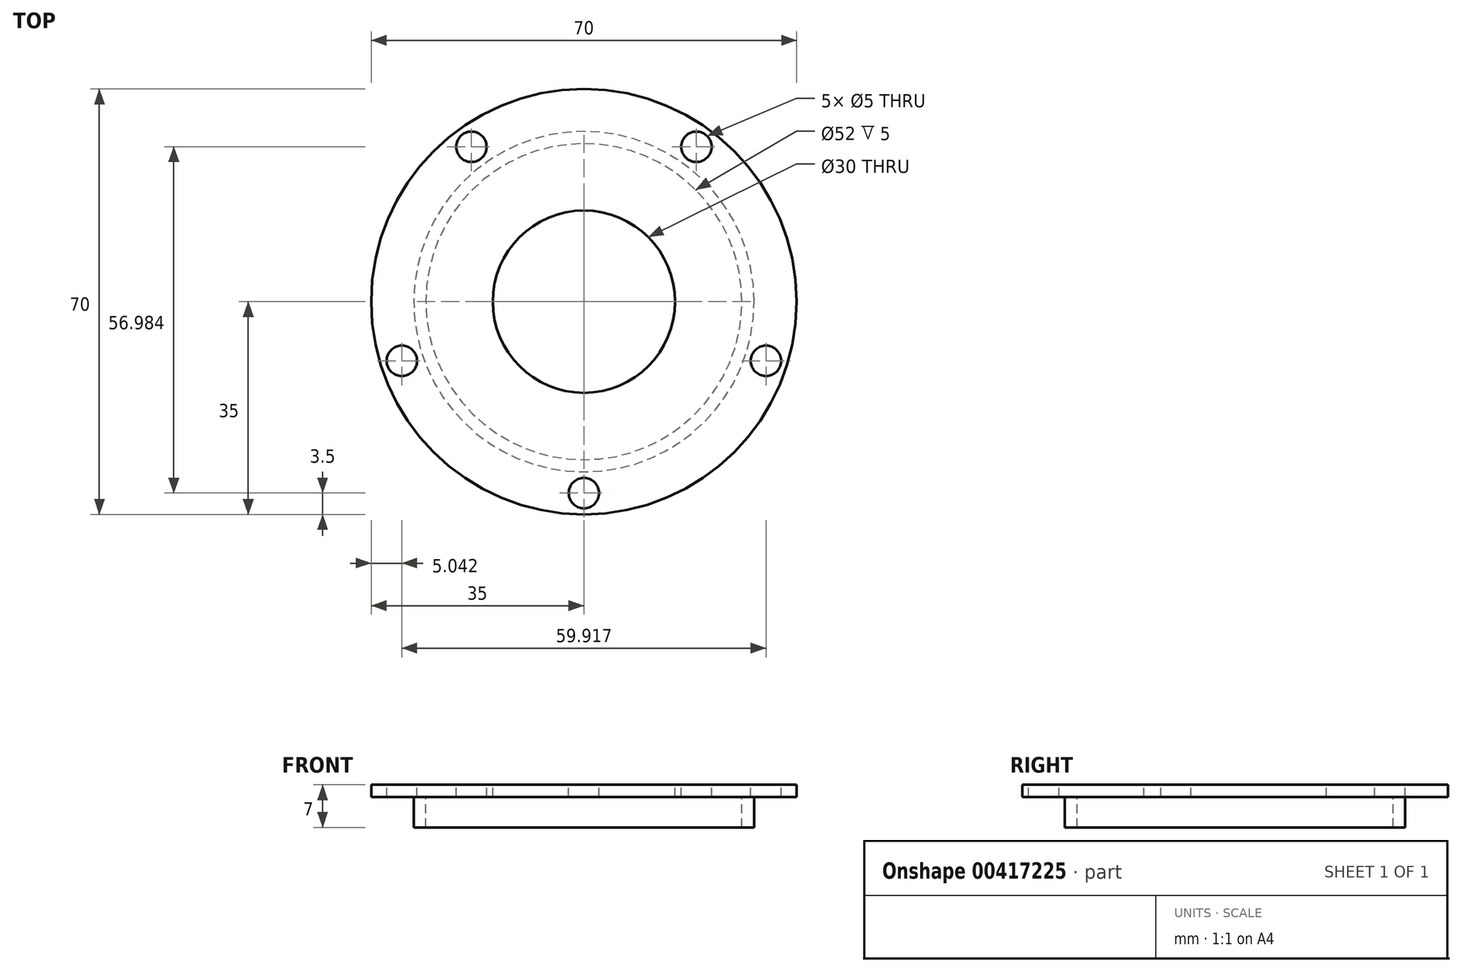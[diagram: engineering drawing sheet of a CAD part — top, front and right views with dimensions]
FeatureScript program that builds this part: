
annotation { "Feature Type Name" : "Feature", "Feature Type Description" : "" }
export const myFeature = defineFeature(function(context is Context, id is Id, definition is map)
    precondition{}
    {
        {
            var Q0;
            Q0=qCreatedBy(makeId("Front.planeOp"),FACE);
            var sketch = newSketch(context, id + "F0", { "sketchPlane" : qUnion([Q0])});
            skLineSegment(sketch, "E0", {"start": v(0, 9.86) * mm, "end": v(0, -12.44) * mm, "construction": true});
            skLineSegment(sketch, "E1", {"start": v(-35, 2) * mm, "end": v(-35, 0) * mm});
            skLineSegment(sketch, "E2", {"start": v(-35, 0) * mm, "end": v(-28, 0) * mm});
            skLineSegment(sketch, "E3", {"start": v(-28, 0) * mm, "end": v(-28, -5) * mm});
            skLineSegment(sketch, "E4", {"start": v(-28, -5) * mm, "end": v(-26, -5) * mm});
            skLineSegment(sketch, "E5", {"start": v(-26, -5) * mm, "end": v(-26, 0) * mm});
            skLineSegment(sketch, "E6", {"start": v(-26, 0) * mm, "end": v(-15, 0) * mm});
            skLineSegment(sketch, "E7", {"start": v(-15, 0) * mm, "end": v(-15, 2) * mm});
            skLineSegment(sketch, "E8", {"start": v(-15, 2) * mm, "end": v(-35, 2) * mm});
            skSolve(sketch);
        }
        {
            var Q0;
            Q0=makeQuery(id+"F0.imprint","IMPRINT",FACE,{"disambiguationData":[TD([[makeQuery(id+"F0.imprint","IMPRINT",EDGE,{"derivedFrom":sQuery(id+"F0.wireOp",EDGE,"E1")}),1.0]])]});
            var Q1;
            Q1=sQuery(id+"F0.wireOp",EDGE,"E0");
            revolve(context, id + "F1", {"entities" : qUnion([Q0]), "axis" : qUnion([Q1]), "revolveType" : RevolveType.FULL});
        }
        {
            var Q0;
            Q0=qCreatedBy(makeId("Top.planeOp"),FACE);
            var sketch = newSketch(context, id + "F2", { "sketchPlane" : qUnion([Q0])});
            skCircle(sketch, "E9", {"center": v(0, 0) * mm, "radius": 31.5 * mm, "construction": true});
            skPoint(sketch, "E10", {"position": v(0, -31.5) * mm});
            skPoint(sketch, "E11.1.0", {"position": v(29.96, -9.73) * mm});
            skPoint(sketch, "E11.2.0", {"position": v(18.52, 25.48) * mm});
            skPoint(sketch, "E11.3.0", {"position": v(-18.52, 25.48) * mm});
            skPoint(sketch, "E11.4.0", {"position": v(-29.96, -9.73) * mm});
            skSolve(sketch);
        }
        {
            var Q0;
            Q0=sQuery(id+"F2.wireOp",VERTEX,"E10");
            var Q1;
            Q1=sQuery(id+"F2.wireOp",VERTEX,"E11.4.0");
            var Q2;
            Q2=sQuery(id+"F2.wireOp",VERTEX,"E11.3.0");
            var Q3;
            Q3=sQuery(id+"F2.wireOp",VERTEX,"E11.2.0");
            var Q4;
            Q4=sQuery(id+"F2.wireOp",VERTEX,"E11.1.0");
            var Q5;
            Q5=makeQuery(id+"F1.opRevolve","SWEPT_BODY",BODY,{"disambiguationData":[OSD([sQuery(id+"F0.wireOp",EDGE,"E1"),sQuery(id+"F0.wireOp",EDGE,"E2"),sQuery(id+"F0.wireOp",EDGE,"E3"),sQuery(id+"F0.wireOp",EDGE,"E4"),sQuery(id+"F0.wireOp",EDGE,"E5"),sQuery(id+"F0.wireOp",EDGE,"E6"),sQuery(id+"F0.wireOp",EDGE,"E7"),sQuery(id+"F0.wireOp",EDGE,"E8")])]});
            hole(context, id + "F3", {"style" : HoleStyle.SIMPLE, "endStyle" : HoleEndStyle.BLIND, "oppositeDirection" : true, "holeDiameter" : 5 * mm, "holeDepth" : 2 * mm, "isTappedThrough" : true, "tappedDepth" : 12 * mm, "tapClearance" : 3, "locations" : qUnion([Q0, Q1, Q2, Q3, Q4]), "scope" : qUnion([Q5]), "startStyle" : HoleStartStyle.PART});
        }
    });
